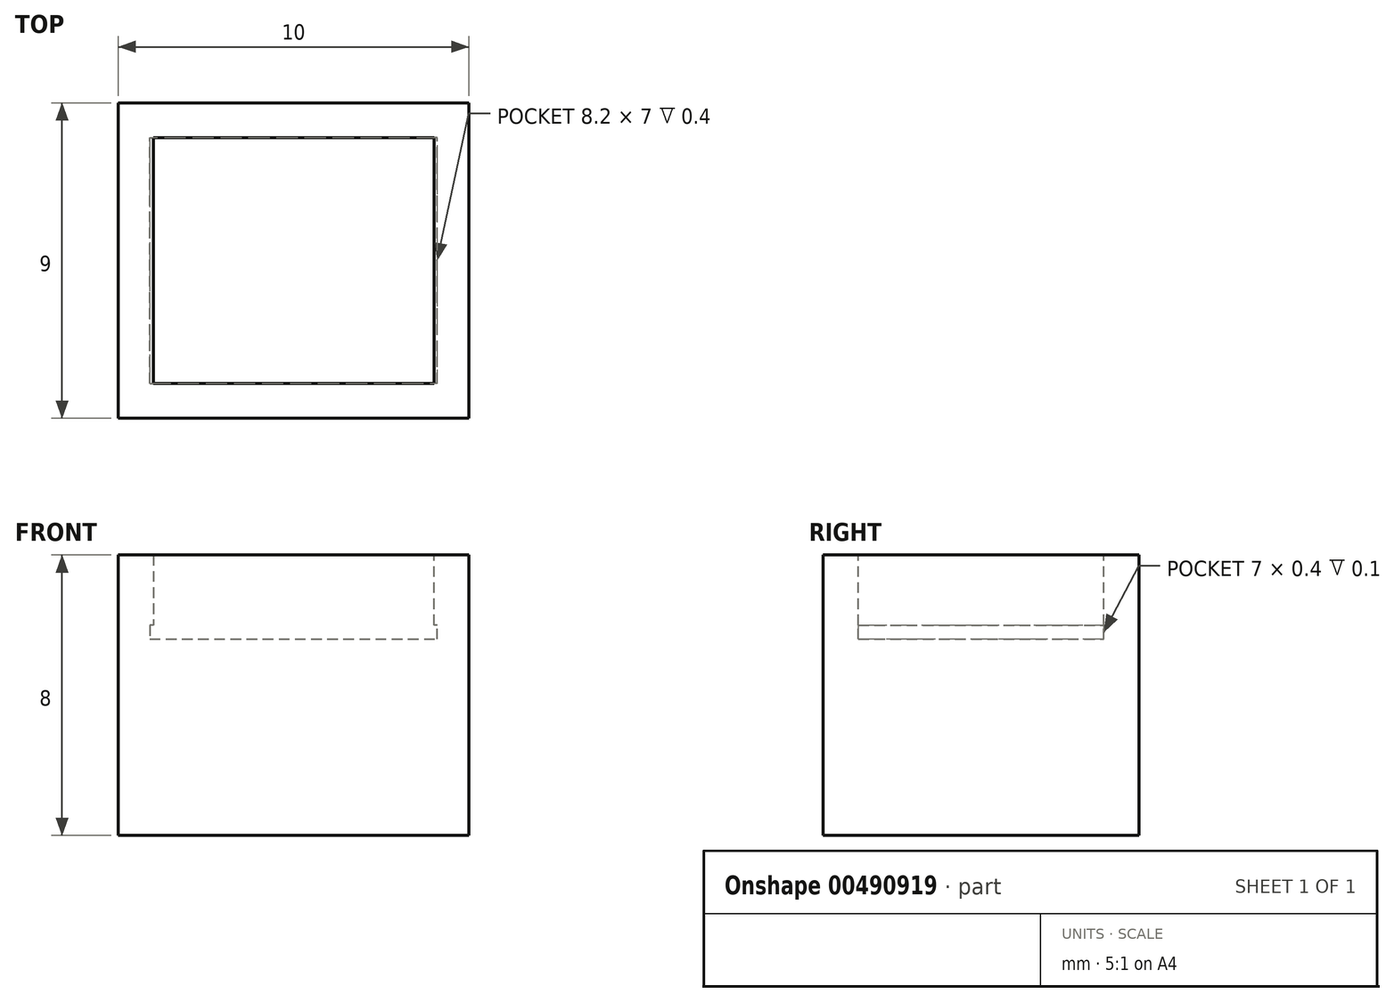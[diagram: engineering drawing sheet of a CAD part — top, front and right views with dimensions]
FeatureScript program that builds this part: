
annotation { "Feature Type Name" : "Feature", "Feature Type Description" : "" }
export const myFeature = defineFeature(function(context is Context, id is Id, definition is map)
    precondition{}
    {
        {
            var Q0;
            Q0=qCreatedBy(makeId("Front.planeOp"),FACE);
            var sketch = newSketch(context, id + "F0", { "sketchPlane" : qUnion([Q0])});
            skLineSegment(sketch, "E0", {"start": v(0, 0) * mm, "end": v(0, 8) * mm});
            skLineSegment(sketch, "E1", {"start": v(0, 8) * mm, "end": v(1, 8) * mm});
            skLineSegment(sketch, "E2", {"start": v(1, 8) * mm, "end": v(1, 6) * mm});
            skLineSegment(sketch, "E3", {"start": v(1, 6) * mm, "end": v(0.9, 6) * mm});
            skLineSegment(sketch, "E4", {"start": v(0.9, 6) * mm, "end": v(0.9, 5.6) * mm});
            skLineSegment(sketch, "E5", {"start": v(0.9, 5.6) * mm, "end": v(9.1, 5.6) * mm});
            skLineSegment(sketch, "E6", {"start": v(9.1, 5.6) * mm, "end": v(9.1, 6) * mm});
            skLineSegment(sketch, "E7", {"start": v(9.1, 6) * mm, "end": v(9, 6) * mm});
            skLineSegment(sketch, "E8", {"start": v(9, 6) * mm, "end": v(9, 8) * mm});
            skLineSegment(sketch, "E9", {"start": v(9, 8) * mm, "end": v(10, 8) * mm});
            skLineSegment(sketch, "E10", {"start": v(10, 8) * mm, "end": v(10, 0) * mm});
            skLineSegment(sketch, "E11", {"start": v(10, 0) * mm, "end": v(0, 0) * mm});
            skSolve(sketch);
        }
        {
            var Q0;
            Q0=makeQuery(id+"F0.imprint","IMPRINT",FACE,{"disambiguationData":[TD([[makeQuery(id+"F0.imprint","IMPRINT",EDGE,{"derivedFrom":sQuery(id+"F0.wireOp",EDGE,"E0")}),-1.0]])]});
            extrude(context, id + "F1", {"entities" : qUnion([Q0]), "depth" : 7 * mm});
        }
        {
            var Q0;
            Q0=makeQuery(id+"F1.opExtrude","CAP_FACE",FACE,{"disambiguationData":[OSD([sQuery(id+"F0.wireOp",EDGE,"E0"),sQuery(id+"F0.wireOp",EDGE,"E1"),sQuery(id+"F0.wireOp",EDGE,"E2"),sQuery(id+"F0.wireOp",EDGE,"E3"),sQuery(id+"F0.wireOp",EDGE,"E4"),sQuery(id+"F0.wireOp",EDGE,"E5"),sQuery(id+"F0.wireOp",EDGE,"E6"),sQuery(id+"F0.wireOp",EDGE,"E7"),sQuery(id+"F0.wireOp",EDGE,"E8"),sQuery(id+"F0.wireOp",EDGE,"E9"),sQuery(id+"F0.wireOp",EDGE,"E10"),sQuery(id+"F0.wireOp",EDGE,"E11")])],"isStart":false});
            var sketch = newSketch(context, id + "F2", { "sketchPlane" : qUnion([Q0])});
            skLineSegment(sketch, "E12.bottom", {"start": v(0, 8) * mm, "end": v(10, 8) * mm});
            skLineSegment(sketch, "E12.top", {"start": v(0, 0) * mm, "end": v(10, 0) * mm});
            skLineSegment(sketch, "E12.left", {"start": v(0, 8) * mm, "end": v(0, 0) * mm});
            skLineSegment(sketch, "E12.right", {"start": v(10, 8) * mm, "end": v(10, 0) * mm});
            skSolve(sketch);
        }
        {
            var Q0;
            Q0=makeQuery(id+"F2.imprint","IMPRINT",FACE,{"disambiguationData":[TD([[makeQuery(id+"F2.imprint","IMPRINT",EDGE,{"derivedFrom":sQuery(id+"F2.wireOp",EDGE,"E12.top")}),-1.0]])]});
            var Q1;
            {var subQ0=makeQuery(id+"F1.opExtrude","CAP_EDGE",EDGE,{"disambiguationData":[OSD([sQuery(id+"F0.wireOp",EDGE,"E2")])],"isStart":false});Q1=makeQuery(id+"F2.imprint","IMPRINT",FACE,{"disambiguationData":[TD([[makeQuery(id+"F2.imprint","IMPRINT",EDGE,{"derivedFrom":subQ0}),1.0]])]});}
            extrude(context, id + "F3", {"entities" : qUnion([Q0, Q1]), "operationType" : NewBodyOperationType.ADD, "depth" : 1 * mm});
        }
        {
            var Q0;
            Q0=makeQuery(id+"F1.opExtrude","CAP_FACE",FACE,{"disambiguationData":[OSD([sQuery(id+"F0.wireOp",EDGE,"E0"),sQuery(id+"F0.wireOp",EDGE,"E1"),sQuery(id+"F0.wireOp",EDGE,"E2"),sQuery(id+"F0.wireOp",EDGE,"E3"),sQuery(id+"F0.wireOp",EDGE,"E4"),sQuery(id+"F0.wireOp",EDGE,"E5"),sQuery(id+"F0.wireOp",EDGE,"E6"),sQuery(id+"F0.wireOp",EDGE,"E7"),sQuery(id+"F0.wireOp",EDGE,"E8"),sQuery(id+"F0.wireOp",EDGE,"E9"),sQuery(id+"F0.wireOp",EDGE,"E10"),sQuery(id+"F0.wireOp",EDGE,"E11")])],"isStart":true});
            var sketch = newSketch(context, id + "F4", { "sketchPlane" : qUnion([Q0])});
            skLineSegment(sketch, "E13.bottom", {"start": v(-10, 8) * mm, "end": v(0, 8) * mm});
            skLineSegment(sketch, "E13.top", {"start": v(-10, 0) * mm, "end": v(0, 0) * mm});
            skLineSegment(sketch, "E13.left", {"start": v(-10, 8) * mm, "end": v(-10, 0) * mm});
            skLineSegment(sketch, "E13.right", {"start": v(0, 8) * mm, "end": v(0, 0) * mm});
            skSolve(sketch);
        }
        {
            var Q0;
            Q0=makeQuery(id+"F4.imprint","IMPRINT",FACE,{"disambiguationData":[TD([[makeQuery(id+"F4.imprint","IMPRINT",EDGE,{"derivedFrom":sQuery(id+"F4.wireOp",EDGE,"E13.top")}),1.0]])]});
            var Q1;
            {var subQ0=makeQuery(id+"F1.opExtrude","CAP_EDGE",EDGE,{"disambiguationData":[OSD([sQuery(id+"F0.wireOp",EDGE,"E2")])],"isStart":true});Q1=makeQuery(id+"F4.imprint","IMPRINT",FACE,{"disambiguationData":[TD([[makeQuery(id+"F4.imprint","IMPRINT",EDGE,{"derivedFrom":subQ0}),-1.0]])]});}
            extrude(context, id + "F5", {"entities" : qUnion([Q0, Q1]), "operationType" : NewBodyOperationType.ADD, "depth" : 1 * mm});
        }
    });
